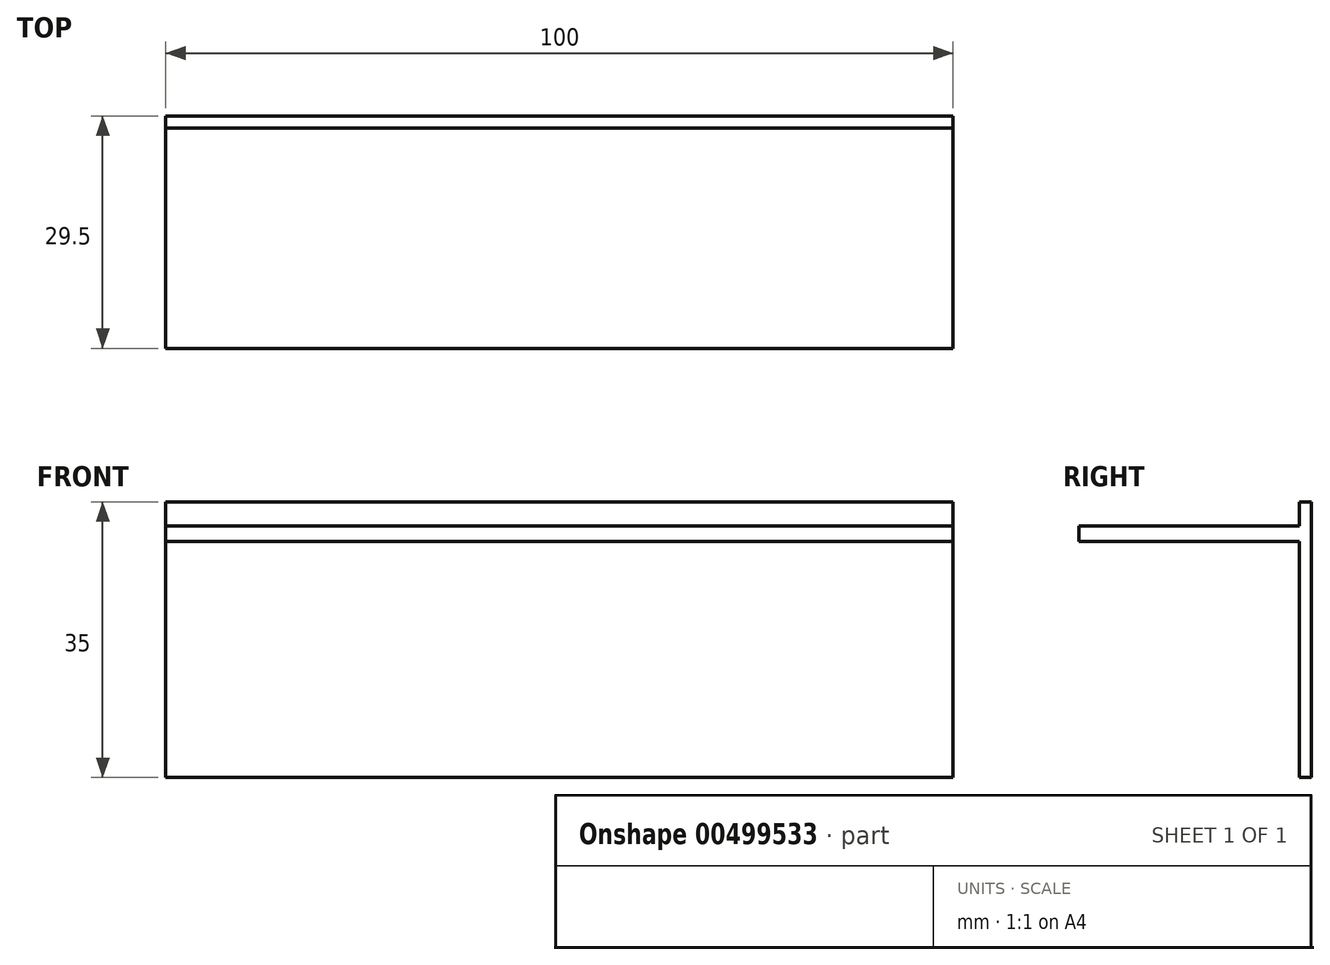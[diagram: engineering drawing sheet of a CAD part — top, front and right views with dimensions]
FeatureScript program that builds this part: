
annotation { "Feature Type Name" : "Feature", "Feature Type Description" : "" }
export const myFeature = defineFeature(function(context is Context, id is Id, definition is map)
    precondition{}
    {
        {
            var Q0;
            Q0=qCreatedBy(makeId("Front.planeOp"),FACE);
            var sketch = newSketch(context, id + "F0", { "sketchPlane" : qUnion([Q0])});
            skLineSegment(sketch, "E0.bottom", {"start": v(50, -17.5) * mm, "end": v(-50, -17.5) * mm});
            skLineSegment(sketch, "E0.top", {"start": v(50, 17.5) * mm, "end": v(-50, 17.5) * mm});
            skLineSegment(sketch, "E0.left", {"start": v(50, -17.5) * mm, "end": v(50, 17.5) * mm});
            skLineSegment(sketch, "E0.right", {"start": v(-50, -17.5) * mm, "end": v(-50, 17.5) * mm});
            skPoint(sketch, "E0.middle", {"position": v(0, 0) * mm});
            skSolve(sketch);
        }
        {
            var Q0;
            Q0 = qSketchRegion(id + "F0", true);
            extrude(context, id + "F1", {"entities" : qUnion([Q0]), "depth" : 1.5 * mm});
        }
        {
            var Q0;
            Q0=makeQuery(id+"F1.opExtrude","CAP_FACE",FACE,{"disambiguationData":[OSD([sQuery(id+"F0.wireOp",EDGE,"E0.bottom"),sQuery(id+"F0.wireOp",EDGE,"E0.top"),sQuery(id+"F0.wireOp",EDGE,"E0.left"),sQuery(id+"F0.wireOp",EDGE,"E0.right")])],"isStart":false});
            var sketch = newSketch(context, id + "F2", { "sketchPlane" : qUnion([Q0])});
            skLineSegment(sketch, "E1.bottom", {"start": v(-50, 14.46) * mm, "end": v(50, 14.46) * mm});
            skLineSegment(sketch, "E1.top", {"start": v(-50, 12.46) * mm, "end": v(50, 12.46) * mm});
            skLineSegment(sketch, "E1.left", {"start": v(-50, 14.46) * mm, "end": v(-50, 12.46) * mm});
            skLineSegment(sketch, "E1.right", {"start": v(50, 14.46) * mm, "end": v(50, 12.46) * mm});
            skSolve(sketch);
        }
        {
            var Q0;
            Q0 = qSketchRegion(id + "F2", true);
            extrude(context, id + "F3", {"entities" : qUnion([Q0]), "operationType" : NewBodyOperationType.ADD, "depth" : 28 * mm});
        }
    });
